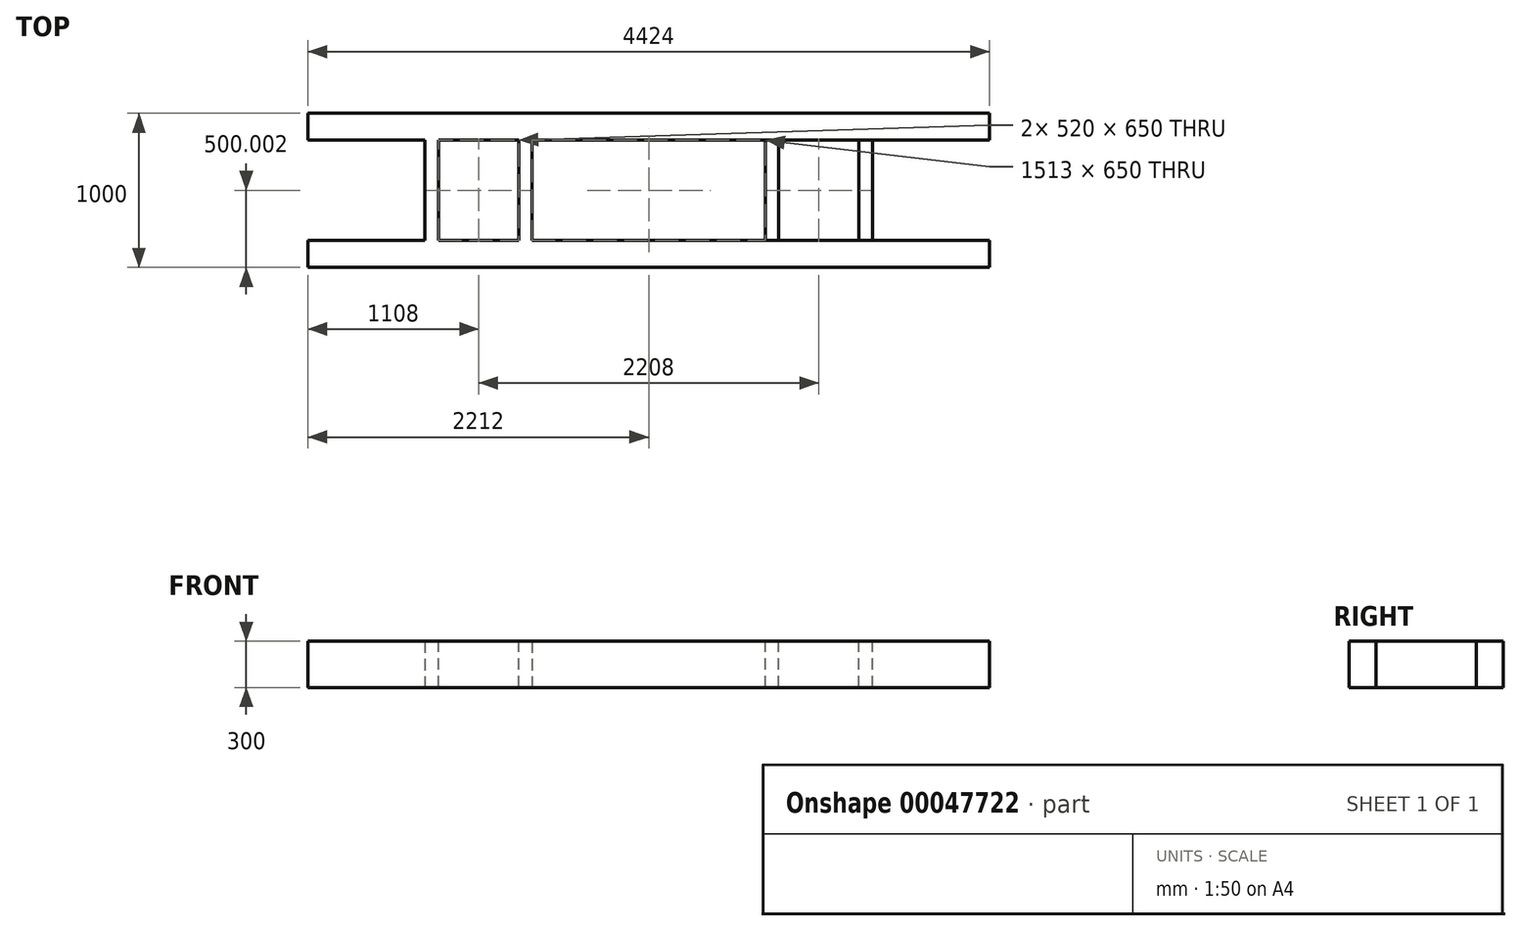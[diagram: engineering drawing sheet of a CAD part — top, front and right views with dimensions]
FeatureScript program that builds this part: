
annotation { "Feature Type Name" : "Feature", "Feature Type Description" : "" }
export const myFeature = defineFeature(function(context is Context, id is Id, definition is map)
    precondition{}
    {
        {
            var Q0;
            Q0=qCreatedBy(makeId("Top.planeOp"),FACE);
            var sketch = newSketch(context, id + "F0", { "sketchPlane" : qUnion([Q0])});
            skLineSegment(sketch, "E0.bottom", {"start": v(-3316.66, -990.23) * mm, "end": v(1107.34, -990.23) * mm});
            skLineSegment(sketch, "E0.top", {"start": v(-3316.66, -1165.23) * mm, "end": v(1107.34, -1165.23) * mm});
            skLineSegment(sketch, "E0.left", {"start": v(-3316.66, -990.23) * mm, "end": v(-3316.66, -1165.23) * mm});
            skLineSegment(sketch, "E1", {"start": v(-3316.66, -990.23) * mm, "end": v(-3316.66, -340.23) * mm, "construction": true});
            skLineSegment(sketch, "E2.bottom", {"start": v(-3316.66, -340.23) * mm, "end": v(1107.34, -340.23) * mm});
            skLineSegment(sketch, "E2.top", {"start": v(-3316.66, -165.23) * mm, "end": v(1107.34, -165.23) * mm});
            skLineSegment(sketch, "E2.left", {"start": v(-3316.66, -340.23) * mm, "end": v(-3316.66, -165.23) * mm});
            skLineSegment(sketch, "E3.bottom", {"start": v(-3316.66, -340.23) * mm, "end": v(-2556.16, -340.23) * mm, "construction": true});
            skLineSegment(sketch, "E3.top", {"start": v(-3316.66, -990.23) * mm, "end": v(-2556.16, -990.23) * mm, "construction": true});
            skLineSegment(sketch, "E3.left", {"start": v(-3316.66, -340.23) * mm, "end": v(-3316.66, -990.23) * mm, "construction": true});
            skLineSegment(sketch, "E3.right", {"start": v(-2556.16, -340.23) * mm, "end": v(-2556.16, -990.23) * mm, "construction": true});
            skLineSegment(sketch, "E4.bottom", {"start": v(-2556.16, -340.23) * mm, "end": v(-1861.16, -340.23) * mm});
            skLineSegment(sketch, "E4.top", {"start": v(-2556.16, -990.23) * mm, "end": v(-1861.16, -990.23) * mm});
            skLineSegment(sketch, "E4.left", {"start": v(-2556.16, -340.23) * mm, "end": v(-2556.16, -990.23) * mm});
            skLineSegment(sketch, "E4.right", {"start": v(-1861.16, -340.23) * mm, "end": v(-1861.16, -990.23) * mm});
            skLineSegment(sketch, "E5.bottom", {"start": v(-2556.16, -340.23) * mm, "end": v(-348.16, -340.23) * mm, "construction": true});
            skLineSegment(sketch, "E5.top", {"start": v(-2556.16, -990.23) * mm, "end": v(-348.16, -990.23) * mm, "construction": true});
            skLineSegment(sketch, "E5.right", {"start": v(-348.16, -340.23) * mm, "end": v(-348.16, -990.23) * mm, "construction": true});
            skLineSegment(sketch, "E6.bottom", {"start": v(-348.16, -340.23) * mm, "end": v(346.84, -340.23) * mm});
            skLineSegment(sketch, "E6.top", {"start": v(-348.16, -990.23) * mm, "end": v(346.84, -990.23) * mm});
            skLineSegment(sketch, "E6.left", {"start": v(-348.16, -340.23) * mm, "end": v(-348.16, -990.23) * mm});
            skLineSegment(sketch, "E6.right", {"start": v(346.84, -340.23) * mm, "end": v(346.84, -990.23) * mm});
            skLineSegment(sketch, "E7.bottom", {"start": v(-348.16, -340.23) * mm, "end": v(1107.34, -340.23) * mm, "construction": true});
            skLineSegment(sketch, "E7.top", {"start": v(-348.16, -990.23) * mm, "end": v(346.84, -990.23) * mm, "construction": true});
            skLineSegment(sketch, "E8.bottom", {"start": v(346.84, -340.23) * mm, "end": v(1107.34, -340.23) * mm, "construction": true});
            skLineSegment(sketch, "E8.top", {"start": v(346.84, -990.23) * mm, "end": v(1107.34, -990.23) * mm, "construction": true});
            skLineSegment(sketch, "E8.left", {"start": v(346.84, -340.23) * mm, "end": v(346.84, -990.23) * mm, "construction": true});
            skLineSegment(sketch, "E8.right", {"start": v(1107.34, -340.23) * mm, "end": v(1107.34, -990.23) * mm, "construction": true});
            skLineSegment(sketch, "E9", {"start": v(1107.34, -990.23) * mm, "end": v(1107.34, -1165.23) * mm});
            skLineSegment(sketch, "E10", {"start": v(1107.34, -340.23) * mm, "end": v(1107.34, -165.23) * mm});
            skSolve(sketch);
        }
        {
            var Q0;
            Q0=qSketchRegion(id+"F0",true);
            extrude(context, id + "F1", {"entities" : qUnion([Q0]), "depth" : 300 * mm});
        }
        {
            var Q0;
            Q0=makeQuery(id+"F1.opExtrude","CAP_FACE",FACE,{"disambiguationData":[OSD([sQuery(id+"F0.wireOp",EDGE,"E0.bottom"),sQuery(id+"F0.wireOp",EDGE,"E0.top"),sQuery(id+"F0.wireOp",EDGE,"E0.left"),sQuery(id+"F0.wireOp",EDGE,"E0.right"),sQuery(id+"F0.wireOp",EDGE,"E2.bottom"),sQuery(id+"F0.wireOp",EDGE,"E2.top"),sQuery(id+"F0.wireOp",EDGE,"E2.left"),sQuery(id+"F0.wireOp",EDGE,"E2.right"),sQuery(id+"F0.wireOp",EDGE,"E4.left"),sQuery(id+"F0.wireOp",EDGE,"E4.right"),sQuery(id+"F0.wireOp",EDGE,"E6.bottom"),sQuery(id+"F0.wireOp",EDGE,"E6.top"),sQuery(id+"F0.wireOp",EDGE,"308fb7c1-f0b3-48d0-ac58-526174caac7e.left"),sQuery(id+"F0.wireOp",EDGE,"308fb7c1-f0b3-48d0-ac58-526174caac7e.right")])],"isStart":false});
            var sketch = newSketch(context, id + "F2", { "sketchPlane" : qUnion([Q0])});
            skLineSegment(sketch, "E11", {"start": v(-2556.16, -340.23) * mm, "end": v(-1861.16, -340.23) * mm, "construction": true});
            skLineSegment(sketch, "E12", {"start": v(-3316.66, -340.23) * mm, "end": v(-1861.16, -340.23) * mm, "construction": true});
            skLineSegment(sketch, "E13", {"start": v(-3316.66, -340.23) * mm, "end": v(-3316.66, -340.23) * mm});
            skLineSegment(sketch, "E14", {"start": v(-2556.16, -990.23) * mm, "end": v(-1861.16, -990.23) * mm, "construction": true});
            skLineSegment(sketch, "E15", {"start": v(-3316.66, -990.23) * mm, "end": v(-3316.66, -990.23) * mm});
            skLineSegment(sketch, "E16.bottom", {"start": v(-2556.16, -340.23) * mm, "end": v(-2468.66, -340.23) * mm, "construction": true});
            skLineSegment(sketch, "E16.top", {"start": v(-2556.16, -990.23) * mm, "end": v(-2468.66, -990.23) * mm, "construction": true});
            skLineSegment(sketch, "E16.left", {"start": v(-2556.16, -340.23) * mm, "end": v(-2556.16, -990.23) * mm, "construction": true});
            skLineSegment(sketch, "E16.right", {"start": v(-2468.66, -340.23) * mm, "end": v(-2468.66, -990.23) * mm, "construction": true});
            skLineSegment(sketch, "E17.bottom", {"start": v(-2468.66, -340.23) * mm, "end": v(-1948.66, -340.23) * mm});
            skLineSegment(sketch, "E17.top", {"start": v(-2468.66, -990.23) * mm, "end": v(-1948.66, -990.23) * mm});
            skLineSegment(sketch, "E17.left", {"start": v(-2468.66, -340.23) * mm, "end": v(-2468.66, -990.23) * mm});
            skLineSegment(sketch, "E17.right", {"start": v(-1948.66, -340.23) * mm, "end": v(-1948.66, -990.23) * mm});
            skLineSegment(sketch, "E18.bottom", {"start": v(-3316.66, -340.23) * mm, "end": v(-3229.16, -340.23) * mm, "construction": true});
            skLineSegment(sketch, "E18.top", {"start": v(-3316.66, -990.23) * mm, "end": v(-3229.16, -990.23) * mm, "construction": true});
            skLineSegment(sketch, "E18.left", {"start": v(-3316.66, -340.23) * mm, "end": v(-3316.66, -990.23) * mm, "construction": true});
            skLineSegment(sketch, "E18.right", {"start": v(-3229.16, -340.23) * mm, "end": v(-3229.16, -990.23) * mm, "construction": true});
            skLineSegment(sketch, "E19.bottom", {"start": v(-3316.66, -340.23) * mm, "end": v(-3404.16, -340.23) * mm, "construction": true});
            skLineSegment(sketch, "E19.top", {"start": v(-3316.66, -990.23) * mm, "end": v(-3404.16, -990.23) * mm, "construction": true});
            skLineSegment(sketch, "E19.right", {"start": v(-3404.16, -340.23) * mm, "end": v(-3404.16, -990.23) * mm, "construction": true});
            skLineSegment(sketch, "E20.bottom", {"start": v(-3404.16, -340.23) * mm, "end": v(-3229.16, -340.23) * mm});
            skLineSegment(sketch, "E20.top", {"start": v(-3404.16, -990.23) * mm, "end": v(-3229.16, -990.23) * mm});
            skLineSegment(sketch, "E20.left", {"start": v(-3229.16, -340.23) * mm, "end": v(-3229.16, -990.23) * mm});
            skLineSegment(sketch, "E20.right", {"start": v(-3404.16, -340.23) * mm, "end": v(-3404.16, -990.23) * mm});
            skSolve(sketch);
        }
        {
            var Q0;
            Q0=qSketchRegion(id+"F2",true);
            extrude(context, id + "F3", {"entities" : qUnion([Q0]), "operationType" : NewBodyOperationType.REMOVE, "endBound" : BoundingType.THROUGH_ALL, "oppositeDirection" : true, "depth" : 25 * mm});
        }
        {
            var Q0;
            Q0=makeQuery(id+"F1.opExtrude","CAP_FACE",FACE,{"disambiguationData":[OSD([sQuery(id+"F0.wireOp",EDGE,"E0.bottom"),sQuery(id+"F0.wireOp",EDGE,"E0.top"),sQuery(id+"F0.wireOp",EDGE,"E0.left"),sQuery(id+"F0.wireOp",EDGE,"E0.right"),sQuery(id+"F0.wireOp",EDGE,"E2.bottom"),sQuery(id+"F0.wireOp",EDGE,"E2.top"),sQuery(id+"F0.wireOp",EDGE,"E2.left"),sQuery(id+"F0.wireOp",EDGE,"E2.right"),sQuery(id+"F0.wireOp",EDGE,"E4.left"),sQuery(id+"F0.wireOp",EDGE,"E4.right"),sQuery(id+"F0.wireOp",EDGE,"E6.bottom"),sQuery(id+"F0.wireOp",EDGE,"E6.top"),sQuery(id+"F0.wireOp",EDGE,"308fb7c1-f0b3-48d0-ac58-526174caac7e.left"),sQuery(id+"F0.wireOp",EDGE,"308fb7c1-f0b3-48d0-ac58-526174caac7e.right")])],"isStart":false});
            var sketch = newSketch(context, id + "F4", { "sketchPlane" : qUnion([Q0])});
            skLineSegment(sketch, "E21.bottom", {"start": v(-2556.16, -340.23) * mm, "end": v(-348.16, -340.23) * mm, "construction": true});
            skLineSegment(sketch, "E21.top", {"start": v(-2556.16, -990.23) * mm, "end": v(-348.16, -990.23) * mm, "construction": true});
            skLineSegment(sketch, "E21.left", {"start": v(-2556.16, -340.23) * mm, "end": v(-2556.16, -990.23) * mm, "construction": true});
            skLineSegment(sketch, "E21.right", {"start": v(-348.16, -340.23) * mm, "end": v(-348.16, -990.23) * mm, "construction": true});
            skLineSegment(sketch, "E22.bottom", {"start": v(-348.16, -340.23) * mm, "end": v(346.84, -340.23) * mm});
            skLineSegment(sketch, "E22.top", {"start": v(-348.16, -990.23) * mm, "end": v(346.84, -990.23) * mm});
            skLineSegment(sketch, "E22.left", {"start": v(-348.16, -340.23) * mm, "end": v(-348.16, -990.23) * mm});
            skLineSegment(sketch, "E22.right", {"start": v(346.84, -340.23) * mm, "end": v(346.84, -990.23) * mm});
            skSolve(sketch);
        }
        {
            var Q0;
            Q0=qSketchRegion(id+"F4",true);
            extrude(context, id + "F5", {"entities" : qUnion([Q0]), "oppositeDirection" : true, "depth" : 300 * mm});
        }
        {
            var Q0;
            Q0=makeQuery(id+"F5.opExtrude","CAP_FACE",FACE,{"disambiguationData":[OSD([sQuery(id+"F4.wireOp",EDGE,"E22.bottom"),sQuery(id+"F4.wireOp",EDGE,"E22.top"),sQuery(id+"F4.wireOp",EDGE,"E22.left"),sQuery(id+"F4.wireOp",EDGE,"E22.right")])],"isStart":true});
            var sketch = newSketch(context, id + "F6", { "sketchPlane" : qUnion([Q0])});
            skLineSegment(sketch, "E23.bottom", {"start": v(-348.16, -340.23) * mm, "end": v(-260.66, -340.23) * mm, "construction": true});
            skLineSegment(sketch, "E23.top", {"start": v(-348.16, -990.23) * mm, "end": v(-260.66, -990.23) * mm, "construction": true});
            skLineSegment(sketch, "E23.left", {"start": v(-348.16, -340.23) * mm, "end": v(-348.16, -990.23) * mm, "construction": true});
            skLineSegment(sketch, "E23.right", {"start": v(-260.66, -340.23) * mm, "end": v(-260.66, -990.23) * mm, "construction": true});
            skLineSegment(sketch, "E24.bottom", {"start": v(346.84, -340.23) * mm, "end": v(259.34, -340.23) * mm, "construction": true});
            skLineSegment(sketch, "E24.top", {"start": v(346.84, -990.23) * mm, "end": v(259.34, -990.23) * mm, "construction": true});
            skLineSegment(sketch, "E24.left", {"start": v(346.84, -340.23) * mm, "end": v(346.84, -990.23) * mm, "construction": true});
            skLineSegment(sketch, "E24.right", {"start": v(259.34, -340.23) * mm, "end": v(259.34, -990.23) * mm, "construction": true});
            skLineSegment(sketch, "E25.bottom", {"start": v(-260.66, -340.23) * mm, "end": v(259.34, -340.23) * mm});
            skLineSegment(sketch, "E25.top", {"start": v(-260.66, -990.23) * mm, "end": v(259.34, -990.23) * mm});
            skLineSegment(sketch, "E25.left", {"start": v(-260.66, -340.23) * mm, "end": v(-260.66, -990.23) * mm});
            skLineSegment(sketch, "E25.right", {"start": v(259.34, -340.23) * mm, "end": v(259.34, -990.23) * mm});
            skSolve(sketch);
        }
        {
            var Q0;
            Q0=qSketchRegion(id+"F6",true);
            extrude(context, id + "F7", {"entities" : qUnion([Q0]), "operationType" : NewBodyOperationType.REMOVE, "endBound" : BoundingType.THROUGH_ALL, "oppositeDirection" : true, "depth" : 25 * mm});
        }
        {
            var Q0;
            Q0=makeQuery(id+"F1.opExtrude","CAP_FACE",FACE,{"disambiguationData":[OSD([sQuery(id+"F0.wireOp",EDGE,"E0.bottom"),sQuery(id+"F0.wireOp",EDGE,"E0.top"),sQuery(id+"F0.wireOp",EDGE,"E0.left"),sQuery(id+"F0.wireOp",EDGE,"E2.bottom"),sQuery(id+"F0.wireOp",EDGE,"E2.top"),sQuery(id+"F0.wireOp",EDGE,"E2.left"),sQuery(id+"F0.wireOp",EDGE,"E4.left"),sQuery(id+"F0.wireOp",EDGE,"E4.right"),sQuery(id+"F0.wireOp",EDGE,"E6.left"),sQuery(id+"F0.wireOp",EDGE,"E6.right"),sQuery(id+"F0.wireOp",EDGE,"E9"),sQuery(id+"F0.wireOp",EDGE,"E10")])],"isStart":false});
            var sketch = newSketch(context, id + "F8", { "sketchPlane" : qUnion([Q0])});
            skPoint(sketch, "E26.0", {"position": v(-260.66, -340.23) * mm});
            skPoint(sketch, "E27.0", {"position": v(259.34, -990.23) * mm});
            skLineSegment(sketch, "E28.bottom", {"start": v(-260.66, -340.23) * mm, "end": v(259.34, -340.23) * mm});
            skLineSegment(sketch, "E28.top", {"start": v(-260.66, -990.23) * mm, "end": v(259.34, -990.23) * mm});
            skLineSegment(sketch, "E28.left", {"start": v(-260.66, -340.23) * mm, "end": v(-260.66, -990.23) * mm});
            skLineSegment(sketch, "E28.right", {"start": v(259.34, -340.23) * mm, "end": v(259.34, -990.23) * mm});
            skSolve(sketch);
        }
        {
            var Q0;
            Q0 = qSketchRegion(id + "F8", true);
            extrude(context, id + "F9", {"entities" : qUnion([Q0]), "operationType" : NewBodyOperationType.REMOVE, "endBound" : BoundingType.THROUGH_ALL, "oppositeDirection" : true, "depth" : 25 * mm});
        }
    });
